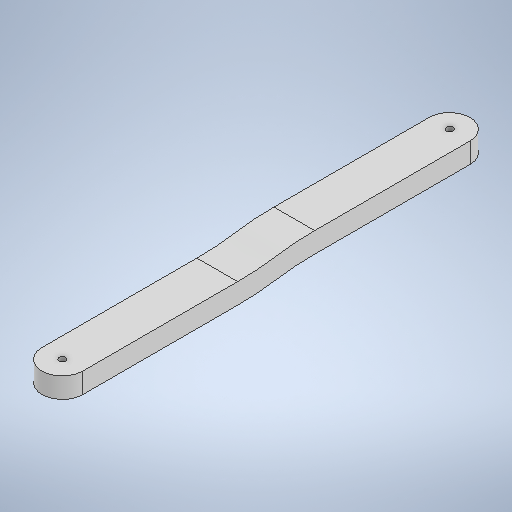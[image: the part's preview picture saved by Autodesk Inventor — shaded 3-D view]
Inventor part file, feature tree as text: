
AUTODESK INVENTOR PART (.ipt)
format: ipt  version: 2025.2 (Build 292293000, 293)  size: 578,560 bytes
history: native  units: in
note: dims shown in document units (in); Inventor stores cm internally (conversion verified against a paired STEP export)
features: other x3, sketch x3, extrude x3, plane x1, loft x1
ambient origin geometry x8: Origin, YZ Plane, XZ Plane, XY Plane, X Axis, Y Axis, Z Axis, Center Point
bodies: Solid1 (feature_tree)
feature tree (11):
  other  "driven_thigh"
  sketch  "Sketch1"  dims[d0=6.7323in d1=3.3661in]
  extrude  "Extrusion1"  Depth=3.3661in
  plane  "Work Plane1"
  extrude  "Extrusion2"  Depth=2.6929in
  loft  "Loft1"
  extrude  "Extrusion3"  Depth=0.3937in
  sketch  "Sketch2"  dims[d2=0.7087in d3=2.6929in]
  other  "Edges1"
  other  "Edges2"
  sketch  "Sketch3"  dims[d4=0.3543in d5=0.0in d6=-0.2559in d7=0.7087in d8=2.7002in d9=0.3543in d10=0.0in d11=0.3937in d12=90.0deg d13=0.3937in d14=90.0deg d15=0.1181in d16=0.1181in d17=0.7087in d18=0.0in]
